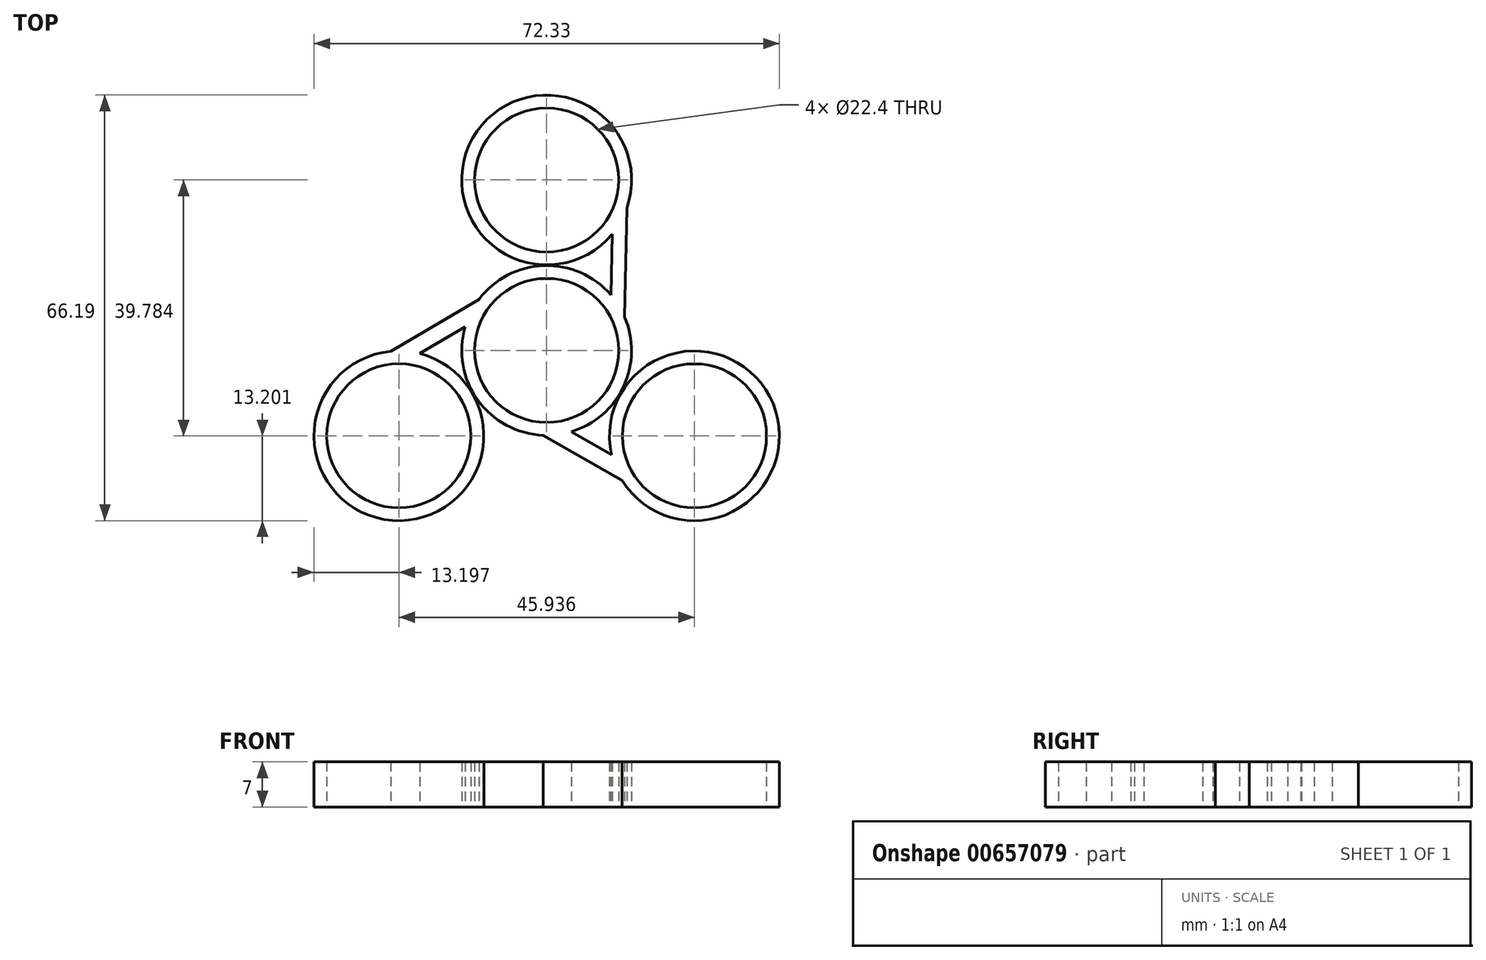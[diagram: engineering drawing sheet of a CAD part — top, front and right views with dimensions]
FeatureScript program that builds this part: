
annotation { "Feature Type Name" : "Feature", "Feature Type Description" : "" }
export const myFeature = defineFeature(function(context is Context, id is Id, definition is map)
    precondition{}
    {
        {
            var Q0;
            Q0=qCreatedBy(makeId("Top.planeOp"),FACE);
            var sketch = newSketch(context, id + "F0", { "sketchPlane" : qUnion([Q0])});
            skCircle(sketch, "E0", {"center": v(0, 0) * mm, "radius": 11.2 * mm});
            skCircle(sketch, "E1", {"center": v(0, 0) * mm, "radius": 13.2 * mm});
            skCircle(sketch, "E2", {"center": v(0, 26.52) * mm, "radius": 11.2 * mm});
            skCircle(sketch, "E3", {"center": v(0, 26.52) * mm, "radius": 13.2 * mm});
            skCircle(sketch, "E4.1.0", {"center": v(-22.97, -13.26) * mm, "radius": 13.2 * mm});
            skCircle(sketch, "E4.1.1", {"center": v(-22.97, -13.26) * mm, "radius": 11.2 * mm});
            skCircle(sketch, "E4.2.0", {"center": v(22.96, -13.27) * mm, "radius": 13.2 * mm});
            skCircle(sketch, "E4.2.1", {"center": v(22.96, -13.27) * mm, "radius": 11.2 * mm});
            skLineSegment(sketch, "E5", {"start": v(-11.1, -7.15) * mm, "end": v(22.75, -26.47) * mm});
            skLineSegment(sketch, "E6", {"start": v(11.9, -5.7) * mm, "end": v(12.62, 30.4) * mm});
            skLineSegment(sketch, "E7", {"start": v(-1.89, 13.06) * mm, "end": v(-33.87, -5.82) * mm});
            skLineSegment(sketch, "E8", {"start": v(9.98, 8.64) * mm, "end": v(10.17, 18.1) * mm});
            skLineSegment(sketch, "E9", {"start": v(-12.67, 3.7) * mm, "end": v(-19.73, -0.47) * mm});
            skLineSegment(sketch, "E10", {"start": v(3.83, -12.63) * mm, "end": v(10.1, -16.2) * mm});
            skSolve(sketch);
        }
        {
            var Q0;
            Q0 = qSketchRegion(id + "F0", true);
            extrude(context, id + "F1", {"entities" : qUnion([Q0]), "depth" : 7 * mm, "offsetDistance" : 25 * mm});
        }
    });
